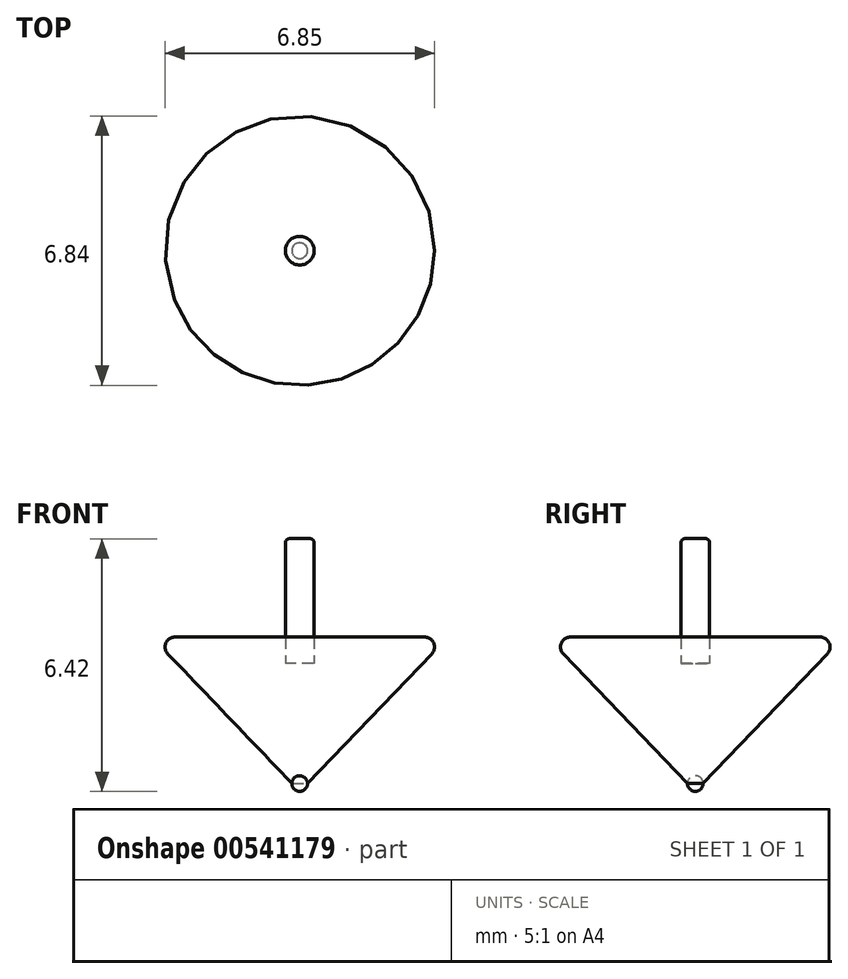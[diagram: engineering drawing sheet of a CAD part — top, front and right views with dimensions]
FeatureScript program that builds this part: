
annotation { "Feature Type Name" : "Feature", "Feature Type Description" : "" }
export const myFeature = defineFeature(function(context is Context, id is Id, definition is map)
    precondition{}
    {
        {
            var Q0;
            Q0=qCreatedBy(makeId("Front.planeOp"),FACE);
            var sketch = newSketch(context, id + "F0", { "sketchPlane" : qUnion([Q0])});
            skLineSegment(sketch, "E0", {"start": v(-0.22, 1.27) * mm, "end": v(-0.02, 1.27) * mm});
            skLineSegment(sketch, "E1.MirrorCS", {"start": v(-0.22, 1.27) * mm, "end": v(-3.78, 5) * mm});
            skLineSegment(sketch, "E2", {"start": v(-3.78, 5) * mm, "end": v(-0.02, 5) * mm});
            skLineSegment(sketch, "E3", {"start": v(-0.02, 1.27) * mm, "end": v(-0.02, 5) * mm});
            skSolve(sketch);
        }
        {
            var Q0;
            Q0=makeQuery(id+"F0.imprint","IMPRINT",FACE,{"disambiguationData":[TD([[makeQuery(id+"F0.imprint","IMPRINT",EDGE,{"derivedFrom":sQuery(id+"F0.wireOp",EDGE,"E1.MirrorCS")}),-1.0]])]});
            var Q1;
            Q1=sQuery(id+"F0.wireOp",EDGE,"E3");
            revolve(context, id + "F1", {"entities" : qUnion([Q0]), "axis" : qUnion([Q1]), "revolveType" : RevolveType.FULL});
        }
        {
            var Q0;
            Q0=qCreatedBy(makeId("Top.planeOp"),FACE);
            var sketch = newSketch(context, id + "F2", { "sketchPlane" : qUnion([Q0])});
            skArc(sketch, "E4", {"start": v(-0.02, 0.2) * mm, "mid": v(-0.22, 0) * mm, "end": v(-0.02, -0.2) * mm});
            skLineSegment(sketch, "E5", {"start": v(-0.02, 0) * mm, "end": v(-0.02, -0.2) * mm});
            skLineSegment(sketch, "E6", {"start": v(-0.02, -0.2) * mm, "end": v(-0.02, 0) * mm});
            skLineSegment(sketch, "E7", {"start": v(-0.02, 0.2) * mm, "end": v(-0.02, 0) * mm});
            skSolve(sketch);
        }
        {
            var Q0;
            Q0=makeQuery(id+"F2.imprint","IMPRINT",FACE,{"disambiguationData":[TD([[makeQuery(id+"F2.imprint","IMPRINT",EDGE,{"derivedFrom":sQuery(id+"F2.wireOp",EDGE,"E4")}),1.0]])]});
            var Q1;
            Q1=sQuery(id+"F2.wireOp",EDGE,"E6");
            revolve(context, id + "F3", {"entities" : qUnion([Q0]), "axis" : qUnion([Q1]), "revolveType" : RevolveType.FULL});
        }
        {
            var Q0;
            Q0=makeQuery(id+"F3.opRevolve","SWEPT_BODY",BODY,{"disambiguationData":[OSD([sQuery(id+"F2.wireOp",EDGE,"E4"),sQuery(id+"F2.wireOp",EDGE,"E6"),sQuery(id+"F2.wireOp",EDGE,"E7")])]});
            transform(context, id + "F4", {"entities" : qUnion([Q0]), "transformType" : TransformType.TRANSLATION_3D, "dx" : 0 * mm, "dy" : 0 * mm, "dz" : 1.27 * mm, "makeCopy" : false});
        }
        {
            var Q0;
            Q0=makeQuery(id+"F1.opRevolve","SWEPT_EDGE",EDGE,{"disambiguationData":[OSD([sQuery(id+"F0.wireOp",EDGE,"E1.MirrorCS"),sQuery(id+"F0.wireOp",EDGE,"E2")])]});
            fillet(context, id + "F5", {"entities" : qUnion([Q0]), "radius" : .25 * mm, "tangentPropagation" : true, "allowEdgeOverflow" : false});
        }
        {
            var Q0;
            Q0=qCreatedBy(makeId("Top.planeOp"),FACE);
            var sketch = newSketch(context, id + "F6", { "sketchPlane" : qUnion([Q0])});
            skCircle(sketch, "E8", {"center": v(-0.02, 0) * mm, "radius": 0.36 * mm});
            skSolve(sketch);
        }
        {
            var Q0;
            Q0=makeQuery(id+"F3.opRevolve","SWEPT_BODY",BODY,{"disambiguationData":[OSD([sQuery(id+"F2.wireOp",EDGE,"E4"),sQuery(id+"F2.wireOp",EDGE,"E6"),sQuery(id+"F2.wireOp",EDGE,"E7")])]});
            var Q1;
            Q1=makeQuery(id+"F1.opRevolve","SWEPT_BODY",BODY,{"disambiguationData":[OSD([sQuery(id+"F0.wireOp",EDGE,"E1.MirrorCS"),sQuery(id+"F0.wireOp",EDGE,"E2"),sQuery(id+"F0.wireOp",EDGE,"E0"),sQuery(id+"F0.wireOp",EDGE,"E3")])]});
            transform(context, id + "F7", {"entities" : qUnion([Q0, Q1]), "transformType" : TransformType.TRANSLATION_3D, "dx" : 0 * mm, "dy" : 0 * mm, "dz" : 0 * mm, "makeCopy" : false});
        }
        {
            var Q0;
            Q0 = qSketchRegion(id + "F6", true);
            extrude(context, id + "F8", {"entities" : qUnion([Q0]), "depth" : 3.17 * mm, "offsetDistance" : 25.4 * mm});
        }
        {
            var Q0;
            Q0=makeQuery(id+"F8.opExtrude","SWEPT_BODY",BODY,{"disambiguationData":[OSD([sQuery(id+"F6.wireOp",EDGE,"E8")])]});
            transform(context, id + "F9", {"entities" : qUnion([Q0]), "transformType" : TransformType.TRANSLATION_3D, "dx" : 0 * mm, "dy" : 0 * mm, "dz" : 4.32 * mm, "makeCopy" : false});
        }
        {
            var Q0;
            Q0=makeQuery(id+"F8.opExtrude","CAP_EDGE",EDGE,{"disambiguationData":[OSD([sQuery(id+"F6.wireOp",EDGE,"E8")])],"isStart":false});
            fillet(context, id + "F10", {"entities" : qUnion([Q0]), "radius" : .1 * mm, "tangentPropagation" : true, "allowEdgeOverflow" : false});
        }
    });
